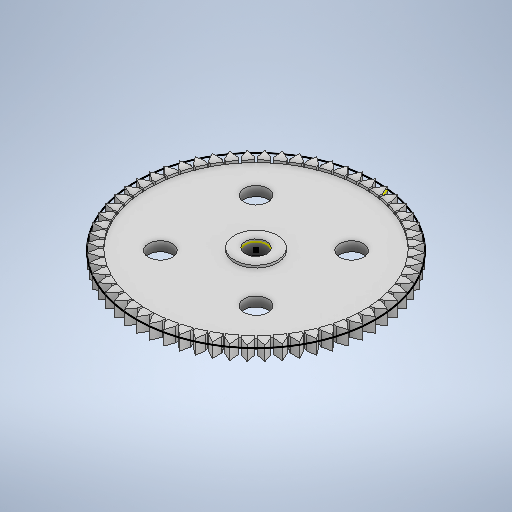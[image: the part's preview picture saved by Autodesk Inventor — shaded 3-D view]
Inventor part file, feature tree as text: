
AUTODESK INVENTOR PART (.ipt)
format: ipt  version: 2025.2 (Build 292293000, 293)  size: 629,248 bytes
history: native  units: mm
features: sketch x4, extrude x3, pattern_circular x1
ambient origin geometry x8: Origin, YZ Plane, XZ Plane, XY Plane, X Axis, Y Axis, Z Axis, Center Point
bodies: Solid1 (feature_tree)
feature tree (8):
  extrude  "Extrusion1"  Depth=45.0mm
  extrude  "Extrusion2"  Depth=4.5mm
  pattern_circular  "Circular Pattern1"  Count=2  [1 undecoded]
  extrude  "Extrusion3"  Depth=5.0mm
  sketch  "Sketch4"  dims[d7=5.0mm d8=5.0mm d9=2.0mm d10=0.0mm d11=50.0mm d12=2.0mm d13=30.0deg d14=2.0mm d15=0.5mm d16=2.5mm d17=0.0mm d18=0.0mm d19=600.0mm d20=360.0deg d22=9.0mm d23=0.5mm d24=2.5mm d25=0.0mm d26=0.0mm]
  sketch  "Sketch1"  dims[d0=50.0mm d1=45.0mm]
  sketch  "Sketch2"  dims[d2=4.5mm d3=20.0mm d4=20.0mm]
  sketch  "Sketch3"  dims[d5=5.0mm d6=5.0mm]
note: 1 required parameter value undecoded (feature->parameter linkage not recoverable at this tier; creation-order binding heuristic only, values carry confidence <= 0.55)
